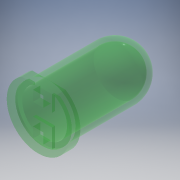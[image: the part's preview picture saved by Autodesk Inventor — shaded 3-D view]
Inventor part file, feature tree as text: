
AUTODESK INVENTOR PART (.ipt)
format: ipt  version: 2019.4 (Build 234330000, 330)  size: 187,904 bytes
history: native  units: mm
features: sketch x2, other x1, revolve x1, plane x1, split x1, extrude x1, shell x1
ambient origin geometry x8: Origin, YZ Plane, XZ Plane, XY Plane, X Axis, Y Axis, Z Axis, Center Point
bodies: Body1 (feature_tree)
feature tree (8):
  other  "Sólido1"
  revolve  "Revolución1"  [1 undecoded]
  plane  "Plano de trabajo1"
  split  "Dividir1"
  extrude  "Extrusión2"  Depth=0.4mm
  shell  "Vaciado1"  Thickness=90.0deg
  sketch  "Boceto1"  dims[d0=2.95mm d1=1.0mm]
  sketch  "Boceto3"  dims[d2=9.7mm d3=5.0mm d5=90.0deg d18=2.5mm d31=1.0mm d32=0.98mm d33=0.98mm d34=1.0mm d35=0.98mm d36=0.0mm d37=0.4mm]
note: 1 required parameter value undecoded (feature->parameter linkage not recoverable at this tier; creation-order binding heuristic only, values carry confidence <= 0.55)
